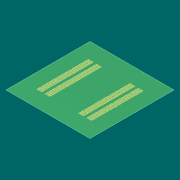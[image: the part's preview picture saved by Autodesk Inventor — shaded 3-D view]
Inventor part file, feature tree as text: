
AUTODESK INVENTOR PART (.ipt)
format: ipt  version: 2016 (Build 200138000, 138)  size: 508,416 bytes
history: native  units: mm
features: extrude x2, pattern_linear x2, sketch x2, mirror x1
ambient origin geometry x8: Origin, YZ Plane, XZ Plane, XY Plane, X Axis, Y Axis, Z Axis, Center Point
bodies: Solid1 (feature_tree), Solid3 (feature_tree)
feature tree (7):
  extrude  "Extrusion1"  Depth=25.8mm
  extrude  "Extrusion3"  Depth=0.25mm
  pattern_linear  "Rectangular Pattern3"  Spacing1=1.5mm  [1 undecoded]
  pattern_linear  "Rectangular Pattern4"  Spacing1=6.9mm  [1 undecoded]
  mirror  "Mirror1"
  sketch  "Sketch1"  dims[d0=25.8mm d1=25.8mm]
  sketch  "Sketch3"  dims[d2=0.01mm d3=0.0mm d24=0.25mm d25=1.5mm d26=6.9mm d27=0.325mm d28=0.01mm d29=0.0mm d30=200.0mm d32=0.4mm d33=1.5mm d34=4.0mm d35=20.0mm d37=8.0mm]
note: 2 required parameter values undecoded (feature->parameter linkage not recoverable at this tier; creation-order binding heuristic only, values carry confidence <= 0.55)
